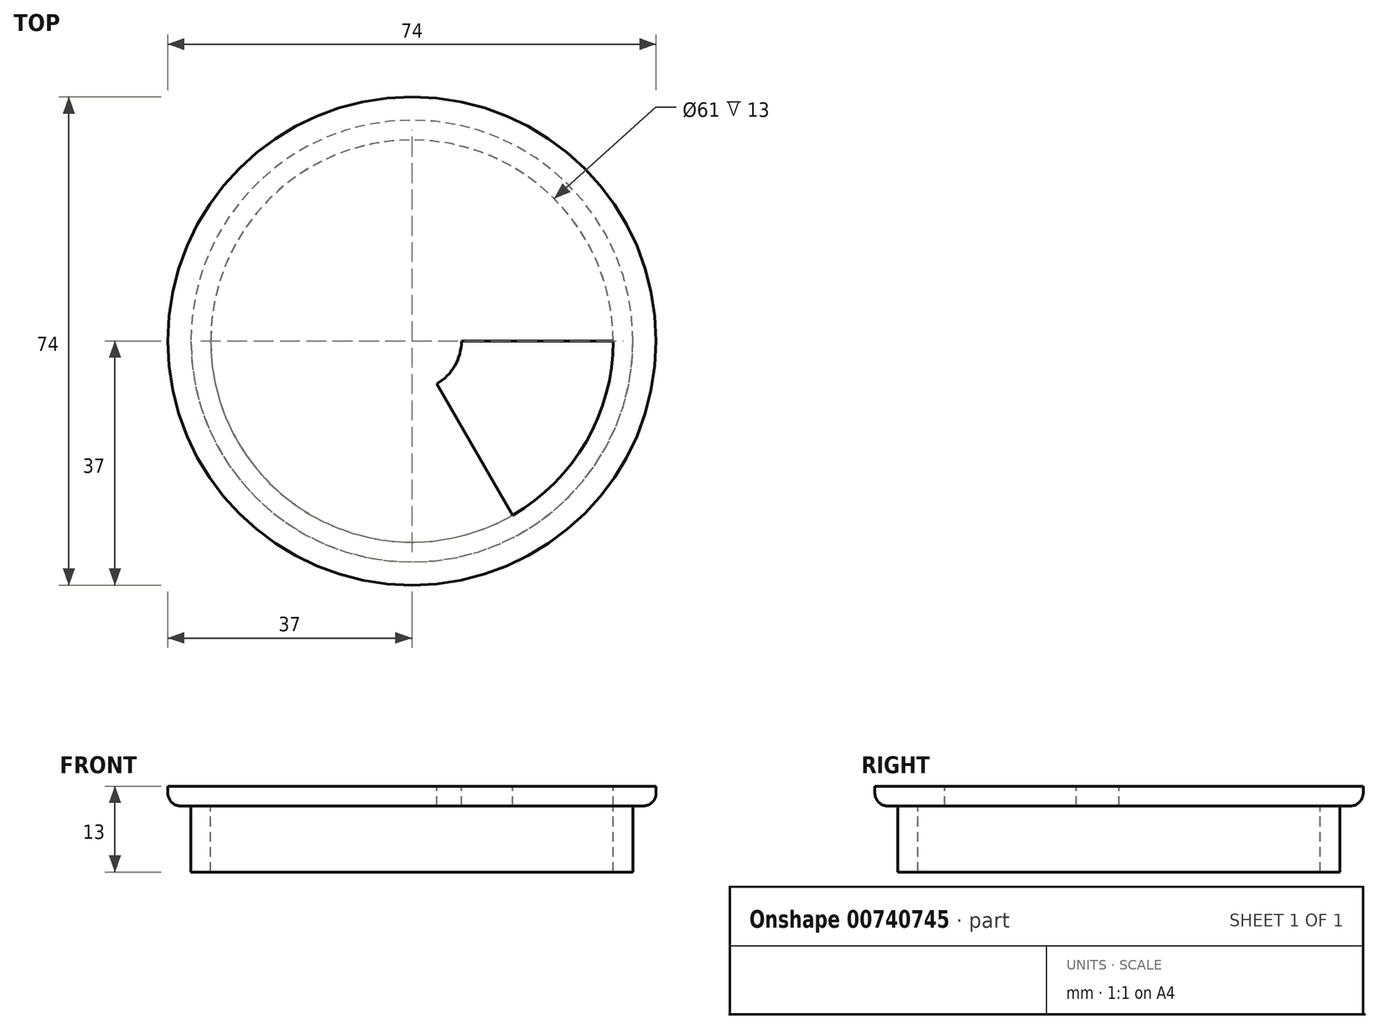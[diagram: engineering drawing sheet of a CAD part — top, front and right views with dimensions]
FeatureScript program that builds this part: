
annotation { "Feature Type Name" : "Feature", "Feature Type Description" : "" }
export const myFeature = defineFeature(function(context is Context, id is Id, definition is map)
    precondition{}
    {
        {
            var Q0;
            Q0=qCreatedBy(makeId("Top.planeOp"),FACE);
            var sketch = newSketch(context, id + "F0", { "sketchPlane" : qUnion([Q0])});
            skCircle(sketch, "E0", {"center": v(0, 0) * mm, "radius": 37 * mm});
            skCircle(sketch, "E1.0", {"center": v(0, 0) * mm, "radius": 33.5 * mm});
            skCircle(sketch, "E2", {"center": v(0, 0) * mm, "radius": 7.5 * mm});
            skLineSegment(sketch, "E3", {"start": v(7.5, 0) * mm, "end": v(33.5, 0) * mm});
            skLineSegment(sketch, "E4.1.0", {"start": v(3.75, -6.5) * mm, "end": v(16.75, -29.01) * mm});
            skLineSegment(sketch, "E4.anchor1", {"start": v(0, 0) * mm, "end": v(7.5, 0) * mm, "construction": true});
            skLineSegment(sketch, "E4.anchor2", {"start": v(0, 0) * mm, "end": v(3.75, -6.5) * mm, "construction": true});
            skCircle(sketch, "E5.0", {"center": v(0, 0) * mm, "radius": 30.5 * mm});
            skSolve(sketch);
        }
        {
            var Q0;
            Q0=makeQuery(id+"F0.imprint","IMPRINT",FACE,{"disambiguationData":[TD([[makeQuery(id+"F0.imprint","IMPRINT",EDGE,{"derivedFrom":sQuery(id+"F0.wireOp",EDGE,"E0")}),1.0]])]});
            var Q1;
            {var subQ0=sQuery(id+"F0.wireOp",EDGE,"E3");Q1=makeQuery(id+"F0.imprint","IMPRINT",FACE,{"disambiguationData":[TD([[makeQuery(id+"F0.imprint","IMPRINT",EDGE,{"derivedFrom":subQ0}),1.0]])]});}
            var Q2;
            {var subQ0=sQuery(id+"F0.wireOp",EDGE,"E2");var subQ1=makeQuery(id+"F0.imprint","INTERSECT",VERTEX,{"derivedFrom":[subQ0,sQuery(id+"F0.wireOp",EDGE,"E3")]});Q2=makeQuery(id+"F0.imprint","IMPRINT",FACE,{"disambiguationData":[TD([[makeQuery(id+"F0.imprint","IMPRINT",EDGE,{"disambiguationData":[TD([[subQ1,-1.0]])],"derivedFrom":subQ0}),1.0]])]});}
            var Q3;
            {var subQ0=sQuery(id+"F0.wireOp",EDGE,"E3");var subQ1=sQuery(id+"F0.wireOp",EDGE,"E1.0");var subQ2=makeQuery(id+"F0.imprint","INTERSECT",VERTEX,{"derivedFrom":[subQ1,subQ0]});Q3=makeQuery(id+"F0.imprint","IMPRINT",FACE,{"disambiguationData":[TD([[makeQuery(id+"F0.imprint","IMPRINT",EDGE,{"disambiguationData":[TD([[subQ2,1.0]])],"derivedFrom":subQ1}),1.0]])]});}
            extrude(context, id + "F1", {"entities" : qUnion([Q0, Q1, Q2, Q3]), "oppositeDirection" : true, "depth" : 3 * mm, "offsetDistance" : 25 * mm});
        }
        {
            var Q0;
            Q0=makeQuery(id+"F1.opExtrude","CAP_EDGE",EDGE,{"disambiguationData":[OSD([sQuery(id+"F0.wireOp",EDGE,"E0")])],"isStart":false});
            fillet(context, id + "F2", {"entities" : qUnion([Q0]), "radius" : 2 * mm, "tangentPropagation" : true, "allowEdgeOverflow" : false});
        }
        {
            var Q0;
            Q0=makeQuery(id+"F1.opExtrude","CAP_FACE",FACE,{"disambiguationData":[OSD([sQuery(id+"F0.wireOp",EDGE,"E0"),sQuery(id+"F0.wireOp",EDGE,"E1.0"),sQuery(id+"F0.wireOp",EDGE,"E2"),sQuery(id+"F0.wireOp",EDGE,"E3"),sQuery(id+"F0.wireOp",EDGE,"E4.1.0")])],"isStart":false});
            var sketch = newSketch(context, id + "F3", { "sketchPlane" : qUnion([Q0])});
            skCircle(sketch, "E6.0", {"center": v(0, 0) * mm, "radius": 33.5 * mm});
            skCircle(sketch, "E7.0", {"center": v(0, 0) * mm, "radius": 30.5 * mm});
            skSolve(sketch);
        }
        {
            var Q0;
            Q0=makeQuery(id+"F3.imprint","IMPRINT",FACE,{"disambiguationData":[TD([[makeQuery(id+"F3.imprint","IMPRINT",EDGE,{"derivedFrom":sQuery(id+"F3.wireOp",EDGE,"E6.0")}),1.0]])]});
            extrude(context, id + "F4", {"entities" : qUnion([Q0]), "operationType" : NewBodyOperationType.ADD, "depth" : 10 * mm, "offsetDistance" : 25 * mm});
        }
    });
